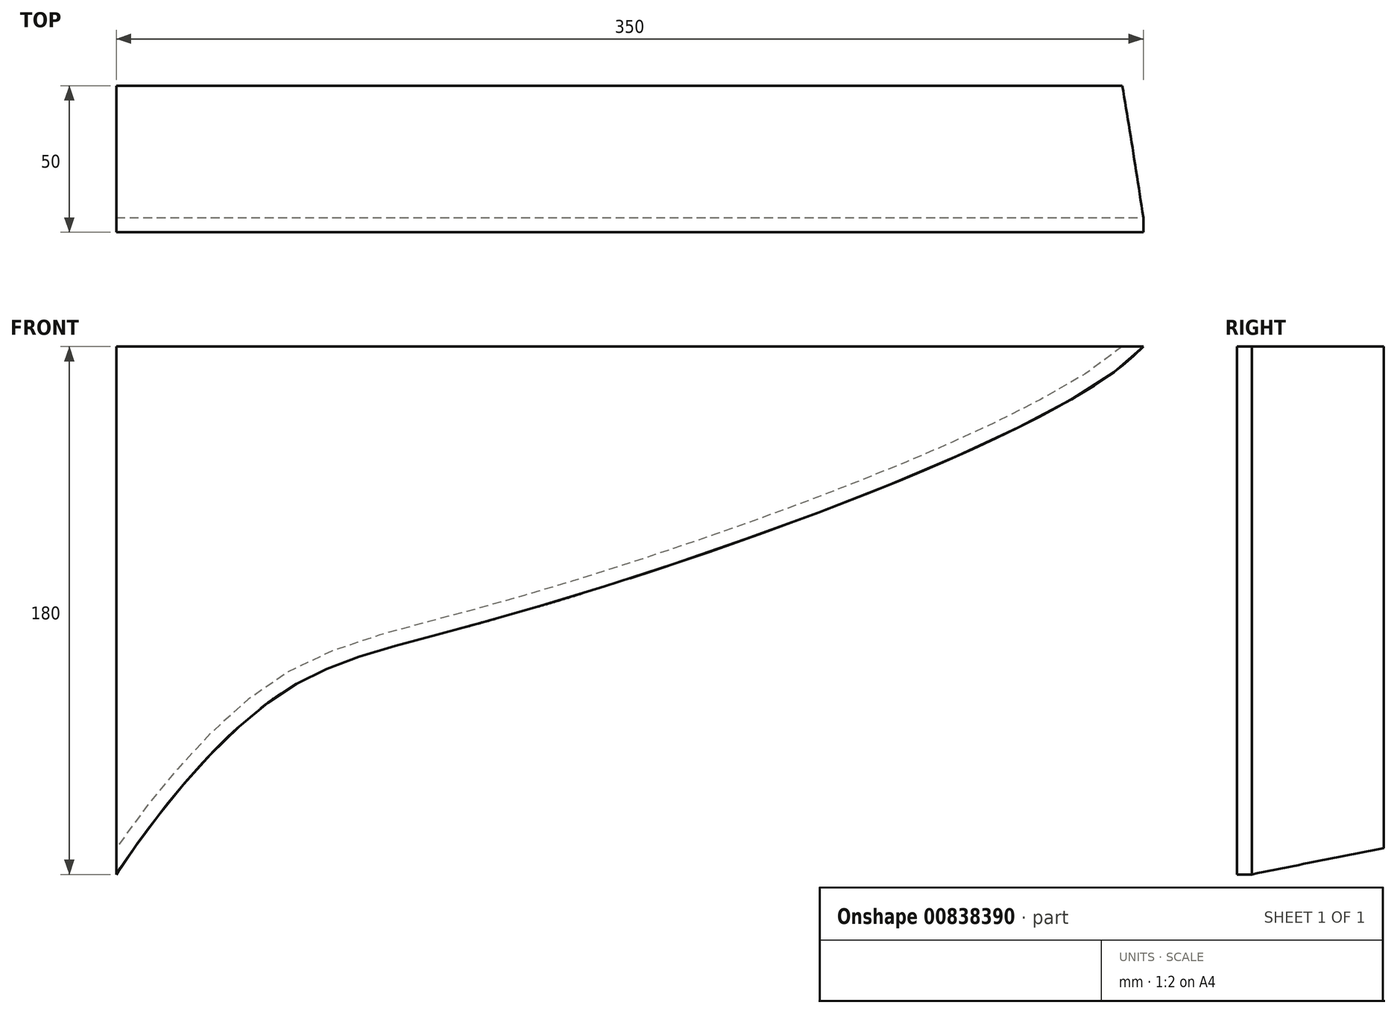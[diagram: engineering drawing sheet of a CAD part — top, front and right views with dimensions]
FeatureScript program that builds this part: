
annotation { "Feature Type Name" : "Feature", "Feature Type Description" : "" }
export const myFeature = defineFeature(function(context is Context, id is Id, definition is map)
    precondition{}
    {
        {
            var Q0;
            Q0=qCreatedBy(makeId("Front.planeOp"),FACE);
            var sketch = newSketch(context, id + "F0", { "sketchPlane" : qUnion([Q0])});
            skLineSegment(sketch, "E0", {"start": v(0, 0) * mm, "end": v(0, 180) * mm});
            skLineSegment(sketch, "E1", {"start": v(0, 180) * mm, "end": v(350, 180) * mm});
            skFitSpline(sketch, "E2", {"points": [v(0, 0) * mm, v(52.6, 59.24) * mm, v(135.5, 88.93) * mm, v(350, 180) * mm], "startDerivative": vector(138.24, 213.16) * mm, "endDerivative": vector(173.58, 192.13) * mm});
            skSolve(sketch);
        }
        {
            var Q0;
            Q0=qSketchRegion(id+"F0",true);
            extrude(context, id + "F1", {"entities" : qUnion([Q0]), "depth" : 50 * mm, "offsetDistance" : 25 * mm});
        }
        {
            var Q0;
            Q0=makeQuery(id+"F1.opExtrude","CAP_EDGE",EDGE,{"disambiguationData":[OSD([sQuery(id+"F0.wireOp",EDGE,"E2")])],"isStart":true});
            chamfer(context, id + "F2", {"entities" : qUnion([Q0]), "chamferType" : ChamferType.TWO_OFFSETS, "width1" : 45 * mm, "oppositeDirection" : false, "width2" : 5 * mm, "tangentPropagation" : true});
        }
    });
